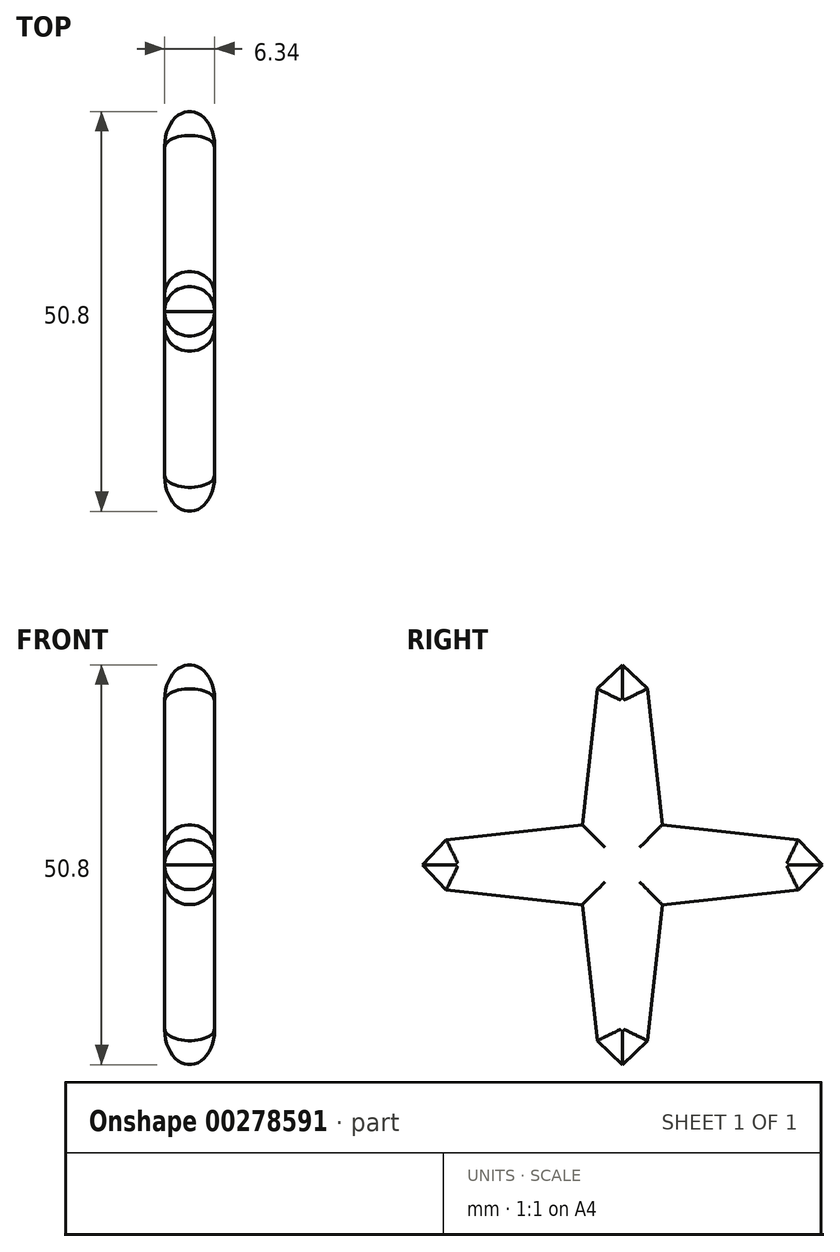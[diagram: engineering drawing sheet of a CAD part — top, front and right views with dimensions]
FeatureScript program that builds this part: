
annotation { "Feature Type Name" : "Feature", "Feature Type Description" : "" }
export const myFeature = defineFeature(function(context is Context, id is Id, definition is map)
    precondition{}
    {
        {
            var Q0;
            Q0=qCreatedBy(makeId("Right.planeOp"),FACE);
            var sketch = newSketch(context, id + "F0", { "sketchPlane" : qUnion([Q0])});
            skLineSegment(sketch, "E0", {"start": v(0, 0) * mm, "end": v(0, 25.4) * mm, "construction": true});
            skLineSegment(sketch, "E1", {"start": v(0, 0) * mm, "end": v(0, -25.4) * mm, "construction": true});
            skLineSegment(sketch, "E2", {"start": v(0, 0) * mm, "end": v(25.4, 0) * mm, "construction": true});
            skLineSegment(sketch, "E3", {"start": v(0, 0) * mm, "end": v(-25.4, 0) * mm, "construction": true});
            skLineSegment(sketch, "E4", {"start": v(0, 0) * mm, "end": v(5.08, 5.08) * mm, "construction": true});
            skLineSegment(sketch, "E5", {"start": v(0, 0) * mm, "end": v(-5.08, 5.08) * mm, "construction": true});
            skLineSegment(sketch, "E6", {"start": v(0, 25.4) * mm, "end": v(-3.18, 22.36) * mm});
            skLineSegment(sketch, "E7", {"start": v(-3.17, 22.36) * mm, "end": v(-5.08, 5.08) * mm});
            skLineSegment(sketch, "E8", {"start": v(0, 25.4) * mm, "end": v(3.18, 22.36) * mm});
            skLineSegment(sketch, "E9", {"start": v(3.17, 22.36) * mm, "end": v(5.08, 5.08) * mm});
            skLineSegment(sketch, "E10.1.0", {"start": v(-22.36, -3.17) * mm, "end": v(-5.08, -5.08) * mm});
            skLineSegment(sketch, "E10.1.1", {"start": v(-22.36, 3.18) * mm, "end": v(-5.08, 5.08) * mm});
            skLineSegment(sketch, "E10.1.2", {"start": v(-25.4, 0) * mm, "end": v(-22.36, -3.17) * mm});
            skLineSegment(sketch, "E10.1.3", {"start": v(-25.4, 0) * mm, "end": v(-22.36, 3.18) * mm});
            skLineSegment(sketch, "E10.2.0", {"start": v(3.17, -22.36) * mm, "end": v(5.08, -5.08) * mm});
            skLineSegment(sketch, "E10.2.1", {"start": v(-3.18, -22.36) * mm, "end": v(-5.08, -5.08) * mm});
            skLineSegment(sketch, "E10.2.2", {"start": v(0, -25.4) * mm, "end": v(3.17, -22.36) * mm});
            skLineSegment(sketch, "E10.2.3", {"start": v(0, -25.4) * mm, "end": v(-3.18, -22.36) * mm});
            skLineSegment(sketch, "E10.3.0", {"start": v(22.36, 3.17) * mm, "end": v(5.08, 5.08) * mm});
            skLineSegment(sketch, "E10.3.1", {"start": v(22.36, -3.18) * mm, "end": v(5.08, -5.08) * mm});
            skLineSegment(sketch, "E10.3.2", {"start": v(25.4, 0) * mm, "end": v(22.36, 3.17) * mm});
            skLineSegment(sketch, "E10.3.3", {"start": v(25.4, 0) * mm, "end": v(22.36, -3.18) * mm});
            skPoint(sketch, "E10.center", {"position": v(0, 0) * mm});
            skSolve(sketch);
        }
        {
            var Q0;
            Q0=makeQuery(id+"F0.imprint","IMPRINT",FACE,{"disambiguationData":[TD([[makeQuery(id+"F0.imprint","IMPRINT",EDGE,{"derivedFrom":sQuery(id+"F0.wireOp",EDGE,"E6")}),1.0]])]});
            extrude(context, id + "F1", {"entities" : qUnion([Q0]), "endBound" : BoundingType.SYMMETRIC, "depth" : 6.35 * mm});
        }
        {
            var Q0;
            Q0=makeQuery(id+"F1.opExtrude","CAP_FACE",FACE,{"disambiguationData":[OSD([sQuery(id+"F0.wireOp",EDGE,"E6"),sQuery(id+"F0.wireOp",EDGE,"E7"),sQuery(id+"F0.wireOp",EDGE,"E8"),sQuery(id+"F0.wireOp",EDGE,"E9"),sQuery(id+"F0.wireOp",EDGE,"E10.1.0"),sQuery(id+"F0.wireOp",EDGE,"E10.1.1"),sQuery(id+"F0.wireOp",EDGE,"E10.1.2"),sQuery(id+"F0.wireOp",EDGE,"E10.1.3"),sQuery(id+"F0.wireOp",EDGE,"E10.2.0"),sQuery(id+"F0.wireOp",EDGE,"E10.2.1"),sQuery(id+"F0.wireOp",EDGE,"E10.2.2"),sQuery(id+"F0.wireOp",EDGE,"E10.2.3"),sQuery(id+"F0.wireOp",EDGE,"E10.3.0"),sQuery(id+"F0.wireOp",EDGE,"E10.3.1"),sQuery(id+"F0.wireOp",EDGE,"E10.3.2"),sQuery(id+"F0.wireOp",EDGE,"E10.3.3")])],"isStart":false});
            var Q1;
            Q1=makeQuery(id+"F1.opExtrude","CAP_FACE",FACE,{"disambiguationData":[OSD([sQuery(id+"F0.wireOp",EDGE,"E6"),sQuery(id+"F0.wireOp",EDGE,"E7"),sQuery(id+"F0.wireOp",EDGE,"E8"),sQuery(id+"F0.wireOp",EDGE,"E9"),sQuery(id+"F0.wireOp",EDGE,"E10.1.0"),sQuery(id+"F0.wireOp",EDGE,"E10.1.1"),sQuery(id+"F0.wireOp",EDGE,"E10.1.2"),sQuery(id+"F0.wireOp",EDGE,"E10.1.3"),sQuery(id+"F0.wireOp",EDGE,"E10.2.0"),sQuery(id+"F0.wireOp",EDGE,"E10.2.1"),sQuery(id+"F0.wireOp",EDGE,"E10.2.2"),sQuery(id+"F0.wireOp",EDGE,"E10.2.3"),sQuery(id+"F0.wireOp",EDGE,"E10.3.0"),sQuery(id+"F0.wireOp",EDGE,"E10.3.1"),sQuery(id+"F0.wireOp",EDGE,"E10.3.2"),sQuery(id+"F0.wireOp",EDGE,"E10.3.3")])],"isStart":true});
            fillet(context, id + "F2", {"entities" : qUnion([Q0, Q1]), "radius" : 3.17 * mm, "tangentPropagation" : true, "allowEdgeOverflow" : false});
        }
    });
